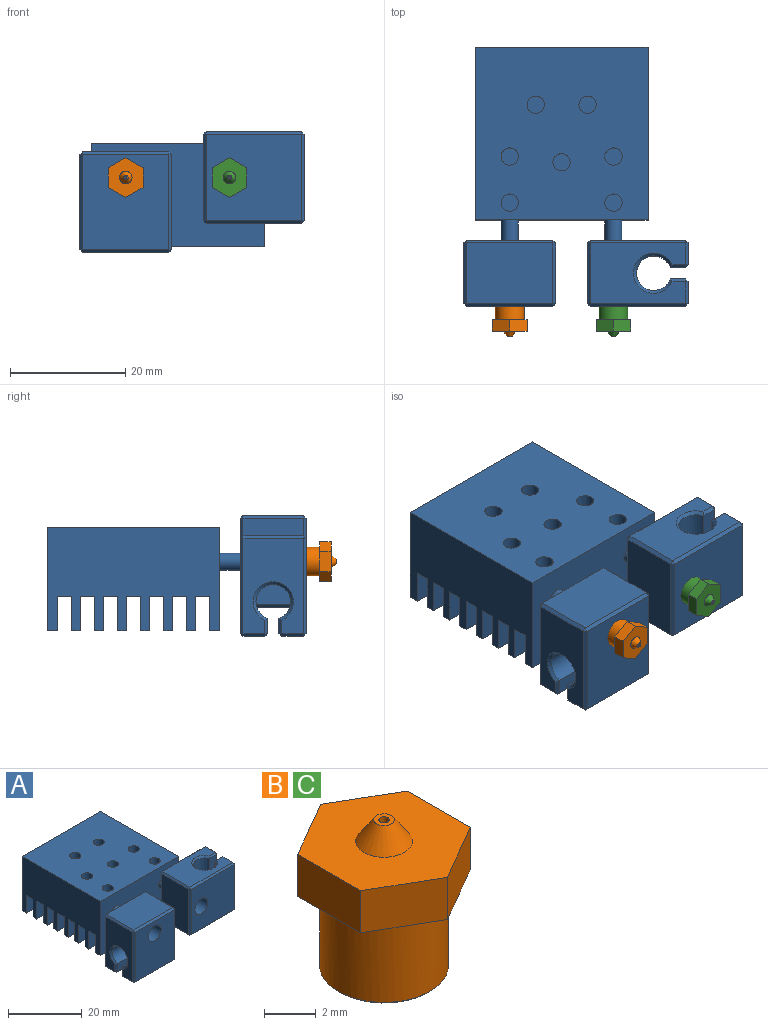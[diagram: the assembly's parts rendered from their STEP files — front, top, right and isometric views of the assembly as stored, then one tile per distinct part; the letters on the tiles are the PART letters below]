
ASSEMBLY  parts=3 mates=2
PART A: 154 faces, bbox 39x45x21 mm
  f0: plane 15x3.75mm, normal (0,0,-1), area 56.2mm2, adj f113,f114,f125,f126
  f1: plane 15x3.75mm, normal (1,0,0), area 56.2mm2, adj f90,f91,f97,f98
  f2: plane 16.5x10.5mm, normal (0,0,-1), area 128.4mm2, adj f69,f71,f75,f80,f81,f86,f91,f92
  f3: plane 30x1.75mm, normal (0,0,-1), area 52.5mm2, adj f10,f11,f13,f38
  f4: plane 30x1.5mm, normal (0,0,-1), area 45mm2, adj f10,f11,f35,f39
  f5: plane 30x1.5mm, normal (0,0,-1), area 45mm2, adj f10,f11,f32,f36
  f6: plane 30x1.5mm, normal (0,0,-1), area 45mm2, adj f10,f11,f29,f33
  f7: plane 30x1.5mm, normal (0,0,-1), area 45mm2, adj f10,f11,f26,f30
  f8: plane 30x1.5mm, normal (0,0,-1), area 45mm2, adj f10,f11,f23,f27
  f9: plane 30x1.5mm, normal (0,0,-1), area 45mm2, adj f10,f11,f20,f24
  f10: plane 30x18mm, normal (-1,0,0), area 435mm2, adj f3,f4,f5,f6,f7,f8,f9,f12
  f11: plane 30x18mm, normal (1,0,0), area 435mm2, adj f3,f4,f5,f6,f7,f8,f9,f12
  f12: plane 30x18mm, normal (0,1,0), area 418.3mm2, adj f10,f11,f14,f15,f16,f18,f43,f46
  f13: plane 30x18mm, normal (0,-1,0), area 526.3mm2, adj f3,f10,f11,f14,f49,f50
  f14: plane 30x30mm, normal (0,0,1), area 850.5mm2, adj f10,f11,f12,f13,f136,f138,f140,f142
  f15: plane 30x1.75mm, normal (0,0,-1), area 52.5mm2, adj f10,f11,f12,f21
  f16: cylinder r=4mm len=8mm, axis (0,1,0), area 163.4mm2, adj f12,f17
  f17: cone r=0mm half-angle=59deg, axis (0,1,0), area 58.6mm2, adj f16
  f18: cylinder r=4mm len=8mm, axis (0,1,0), area 163.4mm2, adj f12,f19
  f19: cone r=0mm half-angle=59deg, axis (0,1,0), area 58.6mm2, adj f18
  f20: plane 30x6mm, normal (0,1,0), area 165.9mm2, adj f9,f10,f11,f22,f42,f45
  f21: plane 30x6mm, normal (0,-1,0), area 165.9mm2, adj f10,f11,f15,f22,f43,f46
  f22: plane 30x2.5mm, normal (0,0,-1), area 75mm2, adj f10,f11,f20,f21
  f23: plane 30x6mm, normal (0,1,0), area 165.9mm2, adj f8,f10,f11,f25,f41,f44
  f24: plane 30x6mm, normal (0,-1,0), area 165.9mm2, adj f9,f10,f11,f25,f42,f45
  f25: plane 30x2.5mm, normal (0,0,-1), area 75mm2, adj f10,f11,f23,f24
  f26: plane 30x6mm, normal (0,1,0), area 180mm2, adj f7,f10,f11,f28
  f27: plane 30x6mm, normal (0,-1,0), area 165.9mm2, adj f8,f10,f11,f28,f41,f44
  f28: plane 30x2.5mm, normal (0,0,-1), area 75mm2, adj f10,f11,f26,f27
  f29: plane 30x6mm, normal (0,1,0), area 180mm2, adj f6,f10,f11,f31
  f30: plane 30x6mm, normal (0,-1,0), area 180mm2, adj f7,f10,f11,f31
  f31: plane 30x2.5mm, normal (0,0,-1), area 75mm2, adj f10,f11,f29,f30
  f32: plane 30x6mm, normal (0,1,0), area 180mm2, adj f5,f10,f11,f34
  f33: plane 30x6mm, normal (0,-1,0), area 180mm2, adj f6,f10,f11,f34
  f34: plane 30x2.5mm, normal (0,0,-1), area 75mm2, adj f10,f11,f32,f33
  f35: plane 30x6mm, normal (0,1,0), area 180mm2, adj f4,f10,f11,f37
  f36: plane 30x6mm, normal (0,-1,0), area 180mm2, adj f5,f10,f11,f37
  f37: plane 30x2.5mm, normal (0,0,-1), area 75mm2, adj f10,f11,f35,f36
  f38: plane 30x6mm, normal (0,1,0), area 180mm2, adj f3,f10,f11,f40
  f39: plane 30x6mm, normal (0,-1,0), area 180mm2, adj f4,f10,f11,f40
  f40: plane 30x2.5mm, normal (0,0,-1), area 75mm2, adj f10,f11,f38,f39
  f41: cylinder r=1.5mm len=3mm, axis (0,1,0), area 14.1mm2, adj f23,f27
  f42: cylinder r=1.5mm len=3mm, axis (0,1,0), area 14.1mm2, adj f20,f24
  f43: cylinder r=1.5mm len=3mm, axis (0,1,0), area 16.5mm2, adj f12,f21
  f44: cylinder r=1.5mm len=3mm, axis (0,1,0), area 14.1mm2, adj f23,f27
  f45: cylinder r=1.5mm len=3mm, axis (0,1,0), area 14.1mm2, adj f20,f24
  f46: cylinder r=1.5mm len=3mm, axis (0,1,0), area 16.5mm2, adj f12,f21
  f47: cylinder r=1.5mm len=10mm, axis (0,1,0), area 94.2mm2, adj f12,f48
  f48: cone r=0mm half-angle=59deg, axis (0,1,0), area 8.2mm2, adj f47
  f49: cylinder r=1.47mm len=3.5mm, axis (0,1,0), area 32.4mm2, adj f13,f55
  f50: cylinder r=1.47mm len=3.5mm, axis (0,1,0), area 32.4mm2, adj f13,f61
  f51: plane 16.5x10.5mm, normal (0,0,1), area 128.4mm2, adj f77,f78,f88,f89,f96,f97,f99,f101
  f52: plane 15x10.5mm, normal (-1,0,0), area 157.5mm2, adj f70,f71,f78,f79
  f53: plane 15x3.75mm, normal (1,0,0), area 56.2mm2, adj f75,f76,f87,f88
  f54: plane 16.5x15mm, normal (0,-1,0), area 227.9mm2, adj f69,f70,f76,f77,f152
  f55: plane 16.5x15mm, normal (0,1,0), area 240.7mm2, adj f49,f79,f80,f89,f90
  f56: plane 16.5x10.5mm, normal (-1,0,0), area 128.4mm2, adj f111,f112,f124,f125,f131,f132,f134,f135
  f57: plane 15x3.75mm, normal (0,0,-1), area 56.2mm2, adj f122,f123,f130,f131
  f58: plane 16.5x10.5mm, normal (1,0,0), area 128.4mm2, adj f103,f105,f109,f114,f115,f116,f121,f122
  f59: plane 15x10.5mm, normal (0,0,1), area 157.5mm2, adj f103,f104,f110,f111
  f60: plane 16.5x15mm, normal (0,-1,0), area 227.9mm2, adj f104,f105,f112,f113,f150
  f61: plane 16.5x15mm, normal (0,1,0), area 240.7mm2, adj f50,f109,f110,f123,f124
  f62: plane 15x2.67mm, normal (0,1,0), area 40.1mm2, adj f64,f81,f87,f96
  f63: plane 15x2.67mm, normal (0,-1,0), area 40.1mm2, adj f64,f92,f98,f101
  f64: cylinder r=3mm len=15mm, axis (0,0,-1), area 252.2mm2, adj f62,f63,f86,f99
  f65: plane 15x2.67mm, normal (0,-1,0), area 40.1mm2, adj f67,f121,f130,f135
  f66: plane 15x2.67mm, normal (0,1,0), area 40.1mm2, adj f67,f115,f126,f132
  f67: cylinder r=3mm len=15mm, axis (-1,0,0), area 252.2mm2, adj f65,f66,f116,f134
  f68: plane 0.5x0.5mm, normal (-0.58,-0.58,-0.58), area 0.2mm2, adj f69,f70,f71
  f69: plane 16.5x0.5mm, normal (0,-0.71,-0.71), area 11.7mm2, adj f2,f54,f68,f72
  f70: plane 15x0.5mm, normal (-0.71,-0.71,0), area 10.6mm2, adj f52,f54,f68,f73
  f71: plane 10.5x0.5mm, normal (-0.71,0,-0.71), area 7.4mm2, adj f2,f52,f68,f74
  f72: plane 0.5x0.5mm, normal (0.58,-0.58,-0.58), area 0.2mm2, adj f69,f75,f76
  f73: plane 0.5x0.5mm, normal (-0.58,-0.58,0.58), area 0.2mm2, adj f70,f77,f78
  f74: plane 0.5x0.5mm, normal (-0.58,0.58,-0.58), area 0.2mm2, adj f71,f79,f80
  f75: plane 3.75x0.5mm, normal (0.71,0,-0.71), area 2.7mm2, adj f2,f53,f72,f82
  f76: plane 15x0.5mm, normal (0.71,-0.71,0), area 10.6mm2, adj f53,f54,f72,f83
  f77: plane 16.5x0.5mm, normal (0,-0.71,0.71), area 11.7mm2, adj f51,f54,f73,f83
  f78: plane 10.5x0.5mm, normal (-0.71,0,0.71), area 7.4mm2, adj f51,f52,f73,f84
  f79: plane 15x0.5mm, normal (-0.71,0.71,0), area 10.6mm2, adj f52,f55,f74,f84
  f80: plane 16.5x0.5mm, normal (0,0.71,-0.71), area 11.7mm2, adj f2,f55,f74,f85
  f81: plane 2.67x0.5mm, normal (0,0.71,-0.71), area 1.8mm2, adj f2,f62,f82,f86
  f82: plane 0.5x0.5mm, normal (0.58,0.58,-0.58), area 0.2mm2, adj f75,f81,f87
  f83: plane 0.5x0.5mm, normal (0.58,-0.58,0.58), area 0.2mm2, adj f76,f77,f88
  f84: plane 0.5x0.5mm, normal (-0.58,0.58,0.58), area 0.2mm2, adj f78,f79,f89
  f85: plane 0.5x0.5mm, normal (0.58,0.58,-0.58), area 0.2mm2, adj f80,f90,f91
  f86: cone r=3mm half-angle=45deg, axis (0,0,-1), area 12.6mm2, adj f2,f64,f81,f92
  f87: plane 15x0.5mm, normal (0.71,0.71,0), area 10.6mm2, adj f53,f62,f82,f93
  f88: plane 3.75x0.5mm, normal (0.71,0,0.71), area 2.7mm2, adj f51,f53,f83,f93
  f89: plane 16.5x0.5mm, normal (0,0.71,0.71), area 11.7mm2, adj f51,f55,f84,f94
  f90: plane 15x0.5mm, normal (0.71,0.71,0), area 10.6mm2, adj f1,f55,f85,f94
  f91: plane 3.75x0.5mm, normal (0.71,0,-0.71), area 2.7mm2, adj f1,f2,f85,f95
  f92: plane 2.67x0.5mm, normal (0,-0.71,-0.71), area 1.8mm2, adj f2,f63,f86,f95
  f93: plane 0.5x0.5mm, normal (0.58,0.58,0.58), area 0.2mm2, adj f87,f88,f96
  f94: plane 0.5x0.5mm, normal (0.58,0.58,0.58), area 0.2mm2, adj f89,f90,f97
  f95: plane 0.5x0.5mm, normal (0.58,-0.58,-0.58), area 0.2mm2, adj f91,f92,f98
  f96: plane 2.67x0.5mm, normal (0,0.71,0.71), area 1.8mm2, adj f51,f62,f93,f99
  f97: plane 3.75x0.5mm, normal (0.71,0,0.71), area 2.7mm2, adj f1,f51,f94,f100
  f98: plane 15x0.5mm, normal (0.71,-0.71,0), area 10.6mm2, adj f1,f63,f95,f100
  f99: cone r=3mm half-angle=45deg, axis (0,0,1), area 12.6mm2, adj f51,f64,f96,f101
  f100: plane 0.5x0.5mm, normal (0.58,-0.58,0.58), area 0.2mm2, adj f97,f98,f101
  f101: plane 2.67x0.5mm, normal (0,-0.71,0.71), area 1.8mm2, adj f51,f63,f99,f100
  f102: plane 0.5x0.5mm, normal (0.58,-0.58,0.58), area 0.2mm2, adj f103,f104,f105
  f103: plane 10.5x0.5mm, normal (0.71,0,0.71), area 7.4mm2, adj f58,f59,f102,f106
  f104: plane 15x0.5mm, normal (0,-0.71,0.71), area 10.6mm2, adj f59,f60,f102,f107
  f105: plane 16.5x0.5mm, normal (0.71,-0.71,0), area 11.7mm2, adj f58,f60,f102,f108
  f106: plane 0.5x0.5mm, normal (0.58,0.58,0.58), area 0.2mm2, adj f103,f109,f110
  f107: plane 0.5x0.5mm, normal (-0.58,-0.58,0.58), area 0.2mm2, adj f104,f111,f112
  f108: plane 0.5x0.5mm, normal (0.58,-0.58,-0.58), area 0.2mm2, adj f105,f113,f114
  f109: plane 16.5x0.5mm, normal (0.71,0.71,0), area 11.7mm2, adj f58,f61,f106,f117
  f110: plane 15x0.5mm, normal (0,0.71,0.71), area 10.6mm2, adj f59,f61,f106,f118
  f111: plane 10.5x0.5mm, normal (-0.71,0,0.71), area 7.4mm2, adj f56,f59,f107,f118
  f112: plane 16.5x0.5mm, normal (-0.71,-0.71,0), area 11.7mm2, adj f56,f60,f107,f119
  f113: plane 15x0.5mm, normal (0,-0.71,-0.71), area 10.6mm2, adj f0,f60,f108,f119
  f114: plane 3.75x0.5mm, normal (0.71,0,-0.71), area 2.7mm2, adj f0,f58,f108,f120
  f115: plane 2.67x0.5mm, normal (0.71,0.71,0), area 1.8mm2, adj f58,f66,f116,f120
  f116: cone r=3.5mm half-angle=45deg, axis (1,0,0), area 12.6mm2, adj f58,f67,f115,f121
  f117: plane 0.5x0.5mm, normal (0.58,0.58,-0.58), area 0.2mm2, adj f109,f122,f123
  f118: plane 0.5x0.5mm, normal (-0.58,0.58,0.58), area 0.2mm2, adj f110,f111,f124
  f119: plane 0.5x0.5mm, normal (-0.58,-0.58,-0.58), area 0.2mm2, adj f112,f113,f125
  f120: plane 0.5x0.5mm, normal (0.58,0.58,-0.58), area 0.2mm2, adj f114,f115,f126
  f121: plane 2.67x0.5mm, normal (0.71,-0.71,0), area 1.8mm2, adj f58,f65,f116,f127
  f122: plane 3.75x0.5mm, normal (0.71,0,-0.71), area 2.7mm2, adj f57,f58,f117,f127
  f123: plane 15x0.5mm, normal (0,0.71,-0.71), area 10.6mm2, adj f57,f61,f117,f128
  f124: plane 16.5x0.5mm, normal (-0.71,0.71,0), area 11.7mm2, adj f56,f61,f118,f128
  f125: plane 3.75x0.5mm, normal (-0.71,0,-0.71), area 2.7mm2, adj f0,f56,f119,f129
  f126: plane 15x0.5mm, normal (0,0.71,-0.71), area 10.6mm2, adj f0,f66,f120,f129
  f127: plane 0.5x0.5mm, normal (0.58,-0.58,-0.58), area 0.2mm2, adj f121,f122,f130
  f128: plane 0.5x0.5mm, normal (-0.58,0.58,-0.58), area 0.2mm2, adj f123,f124,f131
  f129: plane 0.5x0.5mm, normal (-0.58,0.58,-0.58), area 0.2mm2, adj f125,f126,f132
  f130: plane 15x0.5mm, normal (0,-0.71,-0.71), area 10.6mm2, adj f57,f65,f127,f133
  f131: plane 3.75x0.5mm, normal (-0.71,0,-0.71), area 2.7mm2, adj f56,f57,f128,f133
  f132: plane 2.67x0.5mm, normal (-0.71,0.71,0), area 1.8mm2, adj f56,f66,f129,f134
  f133: plane 0.5x0.5mm, normal (-0.58,-0.58,-0.58), area 0.2mm2, adj f130,f131,f135
  f134: cone r=3mm half-angle=45deg, axis (-1,0,0), area 12.6mm2, adj f56,f67,f132,f135
  f135: plane 2.67x0.5mm, normal (-0.71,-0.71,0), area 1.8mm2, adj f56,f65,f133,f134
  f136: cylinder r=1.5mm len=8mm, axis (0,0,1), area 75.4mm2, adj f14,f137
  f137: plane 3x3mm, normal (0,0,1), area 7.1mm2, adj f136
  f138: cylinder r=1.5mm len=8mm, axis (0,0,1), area 75.4mm2, adj f14,f139
  f139: plane 3x3mm, normal (0,0,1), area 7.1mm2, adj f138
  f140: cylinder r=1.5mm len=8mm, axis (0,0,1), area 75.4mm2, adj f14,f141
  f141: plane 3x3mm, normal (0,0,1), area 7.1mm2, adj f140
  f142: cylinder r=1.5mm len=8mm, axis (0,0,1), area 75.4mm2, adj f14,f143
  f143: plane 3x3mm, normal (0,0,1), area 7.1mm2, adj f142
  f144: cylinder r=1.5mm len=8mm, axis (0,0,1), area 75.4mm2, adj f14,f145
  f145: plane 3x3mm, normal (0,0,1), area 7.1mm2, adj f144
  f146: cylinder r=1.5mm len=8mm, axis (0,0,1), area 75.4mm2, adj f14,f147
  f147: plane 3x3mm, normal (0,0,1), area 7.1mm2, adj f146
  f148: cylinder r=1.5mm len=8mm, axis (0,0,1), area 75.4mm2, adj f14,f149
  f149: plane 3x3mm, normal (0,0,1), area 7.1mm2, adj f148
  f150: cylinder r=2.5mm len=6mm, axis (0,-1,0), area 94.2mm2, adj f60,f151
  f151: plane 5x5mm, normal (0,-1,0), area 19.6mm2, adj f150
  f152: cylinder r=2.5mm len=6mm, axis (0,-1,0), area 94.2mm2, adj f54,f153
  f153: plane 5x5mm, normal (0,-1,0), area 19.6mm2, adj f152
PART B: 16 faces, bbox 6x6.9x7 mm
  f0: plane 3.46x2mm, normal (1,0,0), area 6.9mm2, adj f1,f5,f6,f7
  f1: plane 3x2mm, normal (0.5,0.87,0), area 6.9mm2, adj f0,f2,f6,f7
  f2: plane 3x2mm, normal (-0.5,0.87,0), area 6.9mm2, adj f1,f3,f6,f7
  f3: plane 3.46x2mm, normal (-1,0,0), area 6.9mm2, adj f2,f4,f6,f7
  f4: plane 3x2mm, normal (-0.5,-0.87,0), area 6.9mm2, adj f3,f5,f6,f7
  f5: plane 3x2mm, normal (0.5,-0.87,0), area 6.9mm2, adj f0,f4,f6,f7
  f6: plane 6.93x6mm, normal (0,0,1), area 27.4mm2, adj f0,f1,f2,f3,f4,f5,f9
  f7: plane 6.93x6mm, normal (0,0,-1), area 11.5mm2, adj f0,f1,f2,f3,f4,f5,f10
  f8: plane 0.8x0.8mm, normal (0,0,1), area 0.4mm2, adj f9,f13
  f9: cone r=1.1mm half-angle=35deg, axis (0,0,-1), area 5.8mm2, adj f6,f8
  f10: cylinder r=2.5mm len=5mm, axis (0,0,1), area 61.3mm2, adj f7,f12
  f11: plane 4.8x4.8mm, normal (0,0,-1), area 16.3mm2, adj f12,f15
  f12: cone r=2.4mm half-angle=45deg, axis (0,0,1), area 2.2mm2, adj f10,f11
  f13: cylinder r=0.2mm len=0.6mm, axis (0,0,1), area 0.8mm2, adj f8,f14
  f14: cone r=0.2mm half-angle=30deg, axis (0,0,-1), area 3.3mm2, adj f13,f15
  f15: cylinder r=0.75mm len=5.45mm, axis (0,0,-1), area 25.7mm2, adj f11,f14
PART C: same geometry as B
PLACE A at identity fixed
PLACE B rot(axis=(1,0,0),90deg) t=(-9,-32.3,12)mm
PLACE C rot(axis=(1,0,0),90deg) t=(9,-32.3,12)mm
MATE fastened C.f9 <-> A.f49  axis (0,1,0) through (9,-28.4,12)mm
MATE fastened B.f9 <-> A.f50  axis (0,1,0) through (-9,-28.4,12)mm
